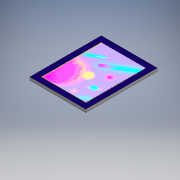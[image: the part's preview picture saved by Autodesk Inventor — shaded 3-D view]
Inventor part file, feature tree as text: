
AUTODESK INVENTOR PART (.ipt)
format: ipt  version: 2016 (Build 200138000, 138)  size: 423,424 bytes
history: native  units: mm
features: sketch x8, extrude x4, chamfer x3, other x3, hole x1, plane x1, loft x1, fillet x1
ambient origin geometry x8: Origin, YZ Plane, XZ Plane, XY Plane, X Axis, Y Axis, Z Axis, Center Point
bodies: Solid1 (feature_tree)
feature tree (22):
  extrude  "Extrusion1"  Depth=365.0mm
  extrude  "Extrusion2"  Depth=30.0mm
  chamfer  "Chamfer1"  Distance=0.5mm
  sketch  "Sketch3"  dims[d5=30.0mm d6=0.5mm d7=0.0mm]
  hole  "Hole1"  [1 undecoded]
  chamfer  "Chamfer2"  Distance=0.5mm Angle=45.0deg
  chamfer  "Chamfer3"  Distance=0.5mm Angle=45.0deg
  sketch  "Sketch5"  dims[d33=75.0mm]
  plane  "Work Plane1"
  sketch  "Sketch6"  dims[d34=83.0mm]
  extrude  "Extrusion3"  Depth=20.0mm
  loft  "Loft1"
  fillet  "Fillet1"  Radius=20.0mm
  extrude  "Extrusion4"  Depth=20.0mm
  sketch  "Sketch1"  dims[d0=286.0mm d1=365.0mm]
  sketch  "Sketch2"  dims[d2=52.0mm d3=0.0mm d4=30.0mm]
  other  "Image2"
  sketch  "Sketch4"  dims[d8=0.5mm d9=2.0mm d10=45.0deg d32=75.0mm]
  sketch  "Sketch7"  dims[d35=140.0mm]
  other  "Edges1"
  other  "Edges2"
  sketch  "Sketch8"  dims[d36=4.917mm d37=12.0mm d38=4.0mm d39=2.0mm d40=90.0deg d41=17.1mm d42=20.594885mm d43=0.5mm d44=2.0mm d45=45.0deg d46=0.5mm d47=2.0mm d48=45.0deg d49=20.0mm d50=20.0mm d51=20.0mm d52=20.0mm d53=-15.0mm d54=10.0mm d55=0.0mm d56=0.0mm d57=90.0deg d58=0.0mm d59=90.0deg d60=5.0mm d61=10.0mm d62=0.0mm]
note: 1 required parameter value undecoded (feature->parameter linkage not recoverable at this tier; creation-order binding heuristic only, values carry confidence <= 0.55)
